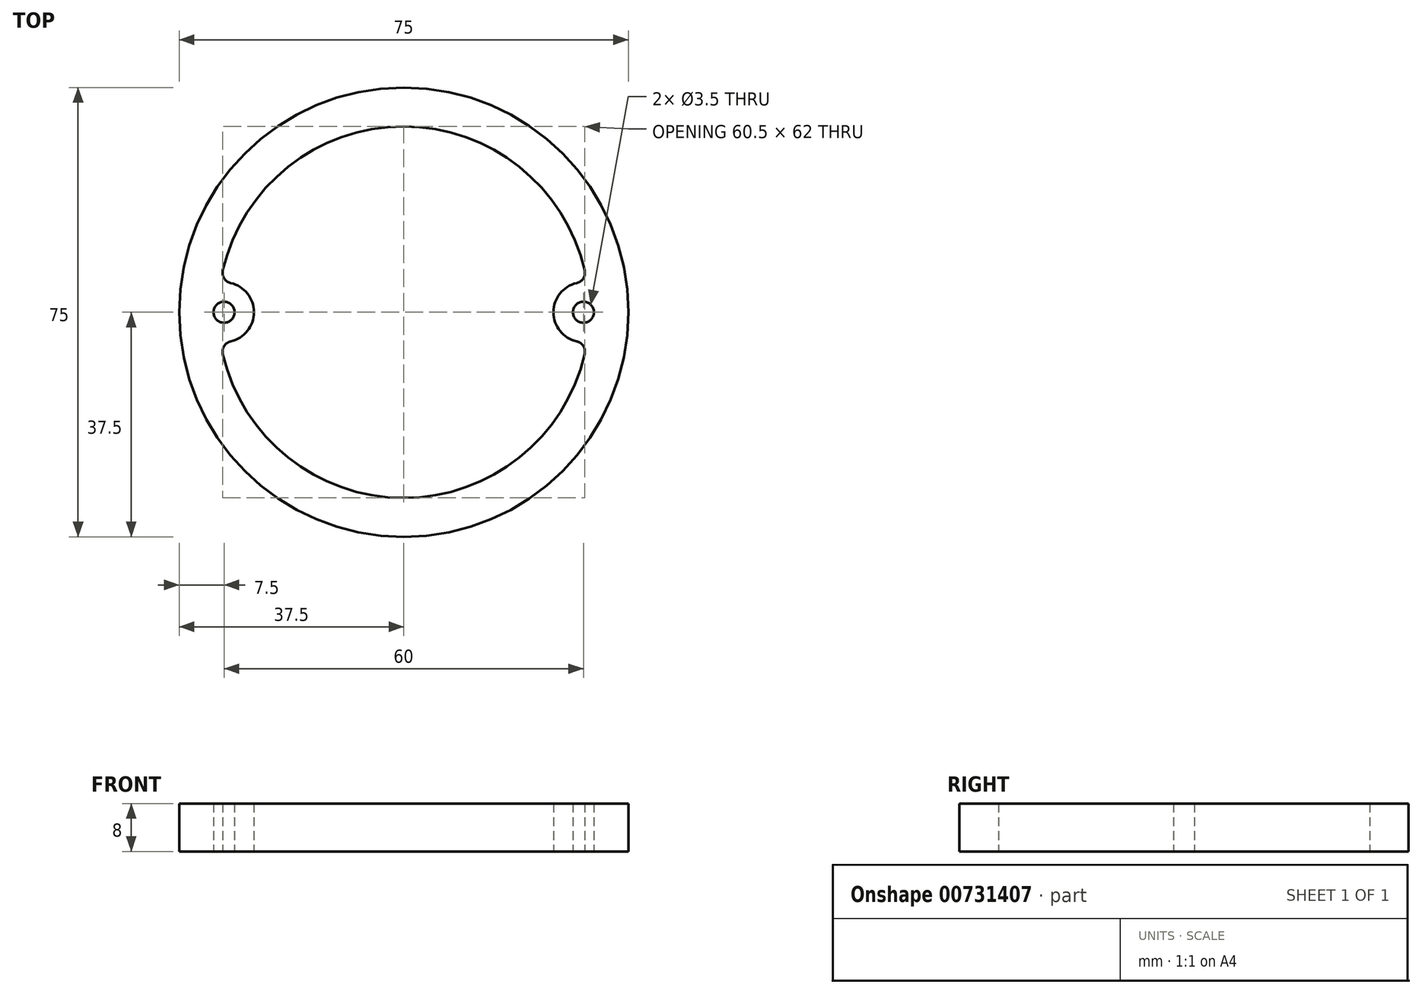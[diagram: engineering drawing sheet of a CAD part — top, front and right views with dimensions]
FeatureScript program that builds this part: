
annotation { "Feature Type Name" : "Feature", "Feature Type Description" : "" }
export const myFeature = defineFeature(function(context is Context, id is Id, definition is map)
    precondition{}
    {
        {
            var Q0;
            Q0=qCreatedBy(makeId("Top.planeOp"),FACE);
            var sketch = newSketch(context, id + "F0", { "sketchPlane" : qUnion([Q0])});
            skCircle(sketch, "E0", {"center": v(0, 0) * mm, "radius": 37.5 * mm});
            skArc(sketch, "E1", {"start": v(-30.2, -6.97) * mm, "mid": v(0, -31) * mm, "end": v(30.2, -6.97) * mm});
            skCircle(sketch, "E2", {"center": v(-30, 0) * mm, "radius": 1.75 * mm});
            skArc(sketch, "E3", {"start": v(-28.89, -4.87) * mm, "mid": v(-25, 0) * mm, "end": v(-28.89, 4.87) * mm});
            skPoint(sketch, "E4.visualSharp", {"position": v(-30.6, 4.96) * mm});
            skArc(sketch, "E4.filletArc", {"start": v(-30.2, 6.97) * mm, "mid": v(-29.98, 5.65) * mm, "end": v(-28.89, 4.87) * mm});
            skPoint(sketch, "E5.visualSharp", {"position": v(-30.6, -4.96) * mm});
            skArc(sketch, "E5.filletArc", {"start": v(-28.89, -4.87) * mm, "mid": v(-29.98, -5.65) * mm, "end": v(-30.2, -6.97) * mm});
            skCircle(sketch, "E6.MirrorC", {"center": v(30, 0) * mm, "radius": 1.75 * mm});
            skArc(sketch, "E7.MirrorCS", {"start": v(28.89, -4.87) * mm, "mid": v(29.98, -5.65) * mm, "end": v(30.2, -6.97) * mm});
            skArc(sketch, "E8.MirrorCS", {"start": v(28.89, -4.87) * mm, "mid": v(25, 0) * mm, "end": v(28.89, 4.87) * mm});
            skArc(sketch, "E9.MirrorCS", {"start": v(30.2, 6.97) * mm, "mid": v(29.98, 5.65) * mm, "end": v(28.89, 4.87) * mm});
            skArc(sketch, "E10.trimOffspring", {"start": v(30.2, 6.97) * mm, "mid": v(0, 31) * mm, "end": v(-30.2, 6.97) * mm});
            skSolve(sketch);
        }
        {
            var Q0;
            Q0 = qSketchRegion(id + "F0", true);
            extrude(context, id + "F1", {"entities" : qUnion([Q0]), "depth" : 8 * mm, "offsetDistance" : 25 * mm});
        }
    });
